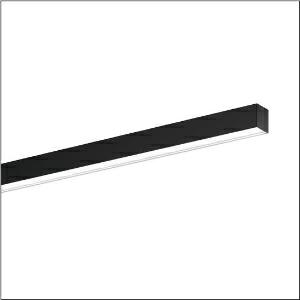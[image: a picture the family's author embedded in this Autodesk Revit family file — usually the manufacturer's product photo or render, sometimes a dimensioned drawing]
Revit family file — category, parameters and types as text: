
# Revit family: silica_21_51mx23da44bb
name_source: partatom
category: Lighting Fixtures
units: mm (PartAtom-declared; Revit-internal decimal feet)

## family parameters
Cut with Voids When Loaded = No
Host = Face
Light Source = No
Part Type = Normal
Room Calculation Point = No
Round Connector Dimension = Use Diameter
Shared = No

## types (1)
- --- (1 x LED, 3280 lm, 22.4 W, 4000K)
    Apparent Load = 22 VA
    CIE Flux Codes = 78 96 99 100 100
    Color Rendering = 80
    Color Temperature = 4000K
    Default Elevation = 1800 mm
    Description = Silica 21, office luminaire, primary optical cover: prismatic diffuser, of PMMA, CAT 2 (L<= 3000cd/m²), light emission: direct distribution, primary light characteristic: symmetric, installation type: surface-mounted, LED, rated luminous flux: 3.280lm, luminous efficacy: 146lm/W, light colour: 840, colour temperature: 4000K, control gear: DALI 2, with terminal, 3+2-pole, max. 2.5mm², mains connection: 220..240V, AC, 50/60Hz, rated input power: 22.4W, luminaire housing, of aluminium, matt jet black (RAL 9005), length: 1.204mm, width: 53mm, height: 53mm, protection rating (complete): IP20, insulation class (complete): insulation class I (protective earthing), certification: CE, permissible operating ambient temperature: 0..+35°C, standard: EN 50419, packaging unit: 1 piece
    Height = 53 mm
    Lamp = 1 x LED
    Lamp Light Flux = 3280 lm
    Lamp Power = 22.4 W
    Lamp count = 1
    Length = 1204 mm
    Luminous efficacy = 146 lm/W
    Manufacturer = Siteco
    ModVariant = No
    Model = 51MX23DA44BB
    Mounting Place = Ceiling
    Mounting Type = Surface mounted
    Number of Poles = 1
    OnlyDefault = Yes
    Power Factor = 1
    Product Name = Silica 21
    Product group = office luminaire | ceiling mounted
    ProductGroupID = 301
    Protection Class = Protection class I
    Protection Degree = IP 20
    RLX_Detail_Level = 1
    RLX_Emergency_Light_Flux = 0 lm
    RLX_Emergency_Type = 0
    RLX_Emergency_Type_DB = No
    RlxData = <blob elided: 23717 chars, md5=fdbaa184>
    Socket = socket
    Standby Power = 0 W
    System Light Flux = 3280 lm
    System Power = 22 W
    Type Comments = factory setting: luminous flux: 100 % | dim-lin: 254 | 323 mA
    Type Image = l_1335925.jpg
    URL = http://relux.com
    VarID = @adj_029765
    Voltage = 0 V
    Weight = 0.00 kg
    Width = 53 mm

## geometry (parser evidence)
native form markers: Blend x4, Sweep x11
no freeform markers — native parametric forms only
